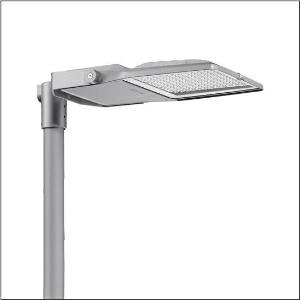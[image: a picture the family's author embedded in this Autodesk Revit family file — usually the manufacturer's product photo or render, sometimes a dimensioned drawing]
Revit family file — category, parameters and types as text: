
# Revit family: floodlight_fl_21_midi___pl33t_5xa7785f2f3a_cf02
name_source: partatom
category: Lighting Fixtures
units: mm (PartAtom-declared; Revit-internal decimal feet)

## family parameters
Cut with Voids When Loaded = No
Host = Face
Light Source = No
Part Type = Normal
Room Calculation Point = No
Round Connector Dimension = Use Diameter
Shared = No

## types (1)
- --- (1 x LED, 35340 lm, 271.6 W, 3000K)
    Apparent Load = 272 VA
    CIE Flux Codes = 26 75 99 100 100
    Color Rendering = 70
    Color Temperature = 3000K
    Default Elevation = 1800 mm
    Description = Floodlight FL 21 midi, floodlight, primary light control with lens, of PMMA, primary optical cover: protective disc, of toughened safety glass, transparent, light distribution: PL33T, light emission: direct distribution, installation type: surface-mounted, LED, High Power LED, rated luminous flux: 35.340lm, luminous efficacy: 130lm/W, light colour: 730, colour temperature: 3000K, control gear: ECG Smart Interface, control: flexible luminous flux parameterisation, time-dependent luminous flux control, constant luminous flux control, overheat protection, pre-setting: logarithmic dimming characteristic, with terminal, 6-pole, mains connection: 220..240V, AC, 50/60Hz, start of lifetime: 272W, end of service life: 287W, reduction: 123W, luminaire housing, of diecast aluminium, powder-coated, Siteco® metallic grey (DB 702S), sealing non-destructively replaceable, please order mast flange separately, mast bracket, of steel, galvanised, powder-coated, Siteco® metallic grey (DB 702S), Smart Interface above, protection rating (complete): IP66, insulation class (complete): insulation class II (safety insulation), certification: CE, ENEC, VDE, protection symbol: D, impact resistance: IK08, permissible operating ambient temperature: -40..+40°C, permissible operating ambient temperature for outdoor applications: -40..+50°C, standard: DIN EN 12944, LABS conformity tested according to VDMA 24364:2018-05, packaging unit: 1 piece

Light Distribution: PL33T
    Height = 76 mm
    Lamp = 1 x LED
    Lamp Light Flux = 35340 lm
    Lamp Power = 271.6 W
    Lamp count = 1
    Length = 657 mm
    Luminous efficacy = 130 lm/W
    Manufacturer = Siteco
    ModVariant = No
    Model = 5XA7785F2F3A
    Number of Poles = 1
    OnlyDefault = Yes
    Power Factor = 1
    Product Name = Floodlight FL 21 midi | PL33T
    Product group = floodlight | pylon annexe
    ProductGroupID = 6200
    Protection Class = Protection class II
    Protection Degree = IP 66
    RLX_Detail_Level = 1
    RLX_Emergency_Light_Flux = 0 lm
    RLX_Emergency_Type = 0
    RLX_Emergency_Type_DB = No
    RlxData = <blob elided: 153401 chars, md5=4a0eac85>
    Socket = socket
    Standby Power = 0 W
    System Light Flux = 35340 lm
    System Power = 272 W
    Type Comments = factory setting: luminous flux: 100 % | dim-lin: 254 | 620 mA
    Type Image = l_1007123.jpg
    URL = http://relux.com
    VarID = @adj_120801
    Voltage = 0 V
    Weight = 0.00 kg
    Width = 442 mm

## geometry (parser evidence)
native form markers: Blend x4, Sweep x13
no freeform markers — native parametric forms only
